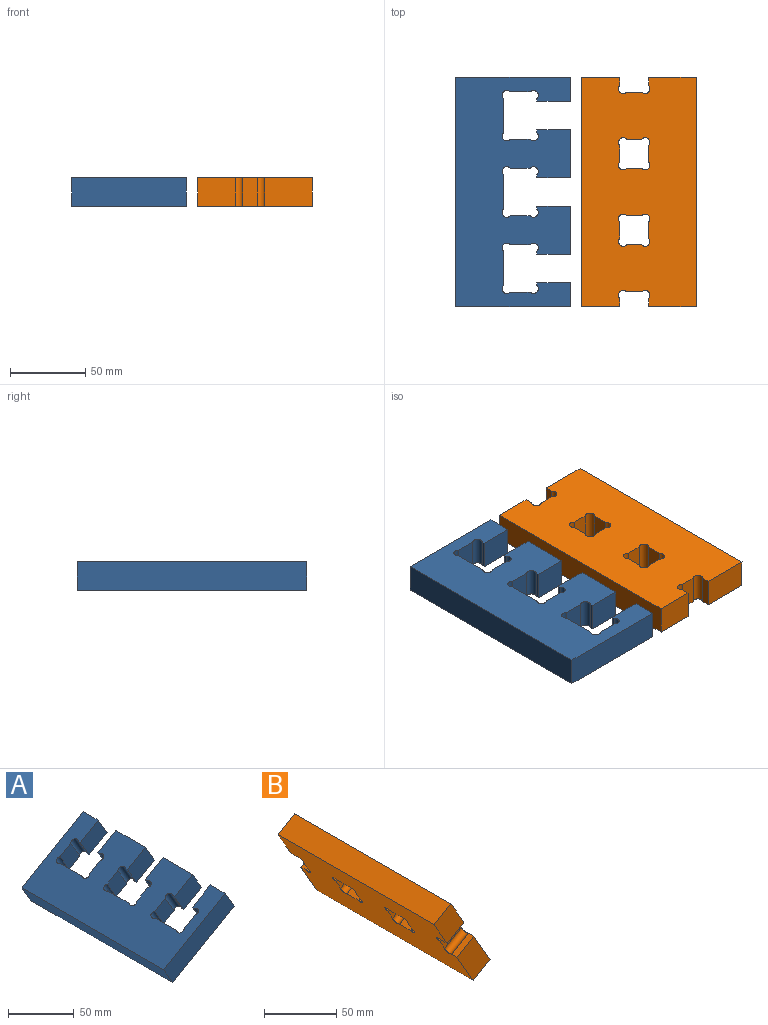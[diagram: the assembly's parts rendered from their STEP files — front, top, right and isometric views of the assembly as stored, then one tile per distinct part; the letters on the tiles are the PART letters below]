
ASSEMBLY  parts=2 mates=3
PART A: 42 faces, bbox 75.5x152.4x54.6 mm
  f0: plane 152.4x65.99mm, normal (-0.5,0,0.87), area 8156.7mm2, adj f2,f3,f4,f5,f6,f7,f8,f9
  f1: plane 152.4x65.99mm, normal (0.5,0,-0.87), area 8156.7mm2, adj f2,f3,f4,f5,f6,f7,f8,f9
  f2: plane 16.5x9.53mm, normal (-0.87,0,-0.5), area 35.4mm2, adj f0,f1,f24,f41
  f3: plane 23.12x21mm, normal (0,1,0), area 252.3mm2, adj f0,f1,f40,f41
  f4: plane 22.77x16.5mm, normal (0.87,0,0.5), area 433.8mm2, adj f0,f1,f39,f40
  f5: plane 23.12x21mm, normal (0,-1,0), area 252.3mm2, adj f0,f1,f38,f39
  f6: plane 16.5x9.53mm, normal (-0.87,0,-0.5), area 35.4mm2, adj f0,f1,f25,f38
  f7: plane 16.5x9.53mm, normal (-0.87,0,-0.5), area 35.4mm2, adj f0,f1,f26,f37
  f8: plane 23.12x21mm, normal (0,1,0), area 252.3mm2, adj f0,f1,f36,f37
  f9: plane 22.77x16.5mm, normal (0.87,0,0.5), area 433.8mm2, adj f0,f1,f35,f36
  f10: plane 23.12x21mm, normal (0,-1,0), area 252.3mm2, adj f0,f1,f34,f35
  f11: plane 16.5x9.53mm, normal (-0.87,0,-0.5), area 35.4mm2, adj f0,f1,f27,f34
  f12: plane 16.5x9.53mm, normal (-0.87,0,-0.5), area 35.4mm2, adj f0,f1,f28,f33
  f13: plane 23.12x21mm, normal (0,1,0), area 252.3mm2, adj f0,f1,f32,f33
  f14: plane 22.77x16.5mm, normal (0.87,0,0.5), area 433.8mm2, adj f0,f1,f31,f32
  f15: plane 23.12x21mm, normal (0,-1,0), area 252.3mm2, adj f0,f1,f30,f31
  f16: plane 16.5x9.53mm, normal (-0.87,0,-0.5), area 35.4mm2, adj f0,f1,f29,f30
  f17: plane 31.75x16.5mm, normal (0.87,0,0.5), area 604.8mm2, adj f0,f1,f26,f29
  f18: plane 31.75x16.5mm, normal (0.87,0,0.5), area 604.8mm2, adj f0,f1,f24,f27
  f19: plane 16.5x15.88mm, normal (0.87,0,0.5), area 302.4mm2, adj f0,f1,f22,f25
  f20: plane 75.52x54.6mm, normal (0,-1,0), area 1451.6mm2, adj f0,f1,f21,f23
  f21: plane 152.4x16.5mm, normal (-0.87,0,-0.5), area 2903.2mm2, adj f0,f1,f20,f22
  f22: plane 75.52x54.6mm, normal (0,1,0), area 1451.6mm2, adj f0,f1,f19,f21
  f23: plane 16.5x15.88mm, normal (0.87,0,0.5), area 302.4mm2, adj f0,f1,f20,f28
  f24: plane 28.77x27.61mm, normal (0,1,0), area 423.4mm2, adj f0,f1,f2,f18
  f25: plane 28.77x27.61mm, normal (0,-1,0), area 423.4mm2, adj f0,f1,f6,f19
  f26: plane 28.77x27.61mm, normal (0,1,0), area 423.4mm2, adj f0,f1,f7,f17
  f27: plane 28.77x27.61mm, normal (0,-1,0), area 423.4mm2, adj f0,f1,f11,f18
  f28: plane 28.77x27.61mm, normal (0,1,0), area 423.4mm2, adj f0,f1,f12,f23
  f29: plane 28.77x27.61mm, normal (0,-1,0), area 423.4mm2, adj f0,f1,f16,f17
  f30: cylinder r=3.17mm len=19.21mm, axis (-0.5,0,0.87), area 190mm2, adj f0,f1,f15,f16
  f31: cylinder r=3.17mm len=19.21mm, axis (-0.5,0,0.87), area 190mm2, adj f0,f1,f14,f15
  f32: cylinder r=3.17mm len=19.21mm, axis (-0.5,0,0.87), area 190mm2, adj f0,f1,f13,f14
  f33: cylinder r=3.17mm len=19.21mm, axis (-0.5,0,0.87), area 190mm2, adj f0,f1,f12,f13
  f34: cylinder r=3.17mm len=19.21mm, axis (-0.5,0,0.87), area 190mm2, adj f0,f1,f10,f11
  f35: cylinder r=3.17mm len=19.21mm, axis (-0.5,0,0.87), area 190mm2, adj f0,f1,f9,f10
  f36: cylinder r=3.17mm len=19.21mm, axis (-0.5,0,0.87), area 190mm2, adj f0,f1,f8,f9
  f37: cylinder r=3.17mm len=19.21mm, axis (-0.5,0,0.87), area 190mm2, adj f0,f1,f7,f8
  f38: cylinder r=3.17mm len=19.21mm, axis (-0.5,0,0.87), area 190mm2, adj f0,f1,f5,f6
  f39: cylinder r=3.17mm len=19.21mm, axis (-0.5,0,0.87), area 190mm2, adj f0,f1,f4,f5
  f40: cylinder r=3.17mm len=19.21mm, axis (-0.5,0,0.87), area 190mm2, adj f0,f1,f3,f4
  f41: cylinder r=3.17mm len=19.21mm, axis (-0.5,0,0.87), area 190mm2, adj f0,f1,f2,f3
PART B: 34 faces, bbox 54.6x152.4x75.5 mm
  f0: plane 16.5x9.53mm, normal (0.5,0,-0.87), area 100.8mm2, adj f16,f17,f20,f33
  f1: plane 16.5x9.53mm, normal (-0.5,0,0.87), area 100.8mm2, adj f15,f16,f17,f32
  f2: plane 21.53x18.25mm, normal (0,1,0), area 191.8mm2, adj f16,f17,f32,f33
  f3: plane 21.53x18.25mm, normal (0,1,0), area 191.8mm2, adj f16,f17,f28,f31
  f4: plane 21.53x18.25mm, normal (0,-1,0), area 191.8mm2, adj f16,f17,f29,f30
  f5: plane 16.5x10.58mm, normal (-0.5,0,0.87), area 201.5mm2, adj f16,f17,f30,f31
  f6: plane 16.5x10.58mm, normal (0.5,0,-0.87), area 201.5mm2, adj f16,f17,f28,f29
  f7: plane 21.53x18.25mm, normal (0,1,0), area 191.8mm2, adj f16,f17,f25,f27
  f8: plane 21.53x18.25mm, normal (0,-1,0), area 191.8mm2, adj f16,f17,f24,f26
  f9: plane 16.5x10.58mm, normal (-0.5,0,0.87), area 201.5mm2, adj f16,f17,f26,f27
  f10: plane 16.5x10.58mm, normal (0.5,0,-0.87), area 201.5mm2, adj f16,f17,f24,f25
  f11: plane 21.53x18.25mm, normal (0,-1,0), area 191.8mm2, adj f16,f17,f22,f23
  f12: plane 16.5x9.53mm, normal (-0.5,0,0.87), area 100.8mm2, adj f14,f16,f17,f23
  f13: plane 16.5x9.53mm, normal (0.5,0,-0.87), area 100.8mm2, adj f16,f17,f18,f22
  f14: plane 37.02x32.37mm, normal (0,-1,0), area 604.8mm2, adj f12,f16,f17,f19
  f15: plane 37.02x32.37mm, normal (0,1,0), area 604.8mm2, adj f1,f16,f17,f19
  f16: plane 152.4x65.99mm, normal (-0.87,0,-0.5), area 10426.1mm2, adj f0,f1,f2,f3,f4,f5,f6,f7
  f17: plane 152.4x65.99mm, normal (0.87,0,0.5), area 10426.1mm2, adj f0,f1,f2,f3,f4,f5,f6,f7
  f18: plane 31.52x29.2mm, normal (0,-1,0), area 483.9mm2, adj f13,f16,f17,f21
  f19: plane 152.4x16.5mm, normal (0.5,0,-0.87), area 2903.2mm2, adj f14,f15,f16,f17
  f20: plane 31.52x29.2mm, normal (0,1,0), area 483.9mm2, adj f0,f16,f17,f21
  f21: plane 152.4x16.5mm, normal (-0.5,0,0.87), area 2903.2mm2, adj f16,f17,f18,f20
  f22: cylinder r=3.17mm len=19.21mm, axis (0.87,0,0.5), area 190mm2, adj f11,f13,f16,f17
  f23: cylinder r=3.17mm len=19.21mm, axis (0.87,0,0.5), area 190mm2, adj f11,f12,f16,f17
  f24: cylinder r=3.17mm len=19.21mm, axis (0.87,0,0.5), area 190mm2, adj f8,f10,f16,f17
  f25: cylinder r=3.17mm len=19.21mm, axis (0.87,0,0.5), area 190mm2, adj f7,f10,f16,f17
  f26: cylinder r=3.17mm len=19.21mm, axis (0.87,0,0.5), area 190mm2, adj f8,f9,f16,f17
  f27: cylinder r=3.17mm len=19.21mm, axis (0.87,0,0.5), area 190mm2, adj f7,f9,f16,f17
  f28: cylinder r=3.17mm len=19.21mm, axis (0.87,0,0.5), area 190mm2, adj f3,f6,f16,f17
  f29: cylinder r=3.17mm len=19.21mm, axis (0.87,0,0.5), area 190mm2, adj f4,f6,f16,f17
  f30: cylinder r=3.17mm len=19.21mm, axis (0.87,0,0.5), area 190mm2, adj f4,f5,f16,f17
  f31: cylinder r=3.17mm len=19.21mm, axis (0.87,0,0.5), area 190mm2, adj f3,f5,f16,f17
  f32: cylinder r=3.17mm len=19.21mm, axis (0.87,0,0.5), area 190mm2, adj f1,f2,f16,f17
  f33: cylinder r=3.17mm len=19.21mm, axis (0.87,0,0.5), area 190mm2, adj f0,f2,f16,f17
PLACE A rot(axis=(0,1,0),30deg) t=(113.68,153.53,0)mm
PLACE B rot(axis=(0,-1,0),60deg) t=(128.27,153.53,81.93)mm
MATE planar A.f20 <-> B.f14  axis (0,-1,0) through (38.1,0,19.05)mm
MATE parallel B.f19 <-> A.f21  axis (1,0,0) through (160.02,76.2,9.53)mm
MATE planar B.f16 <-> A.f1  axis (0,0,-1) through (160.02,76.2,0)mm
